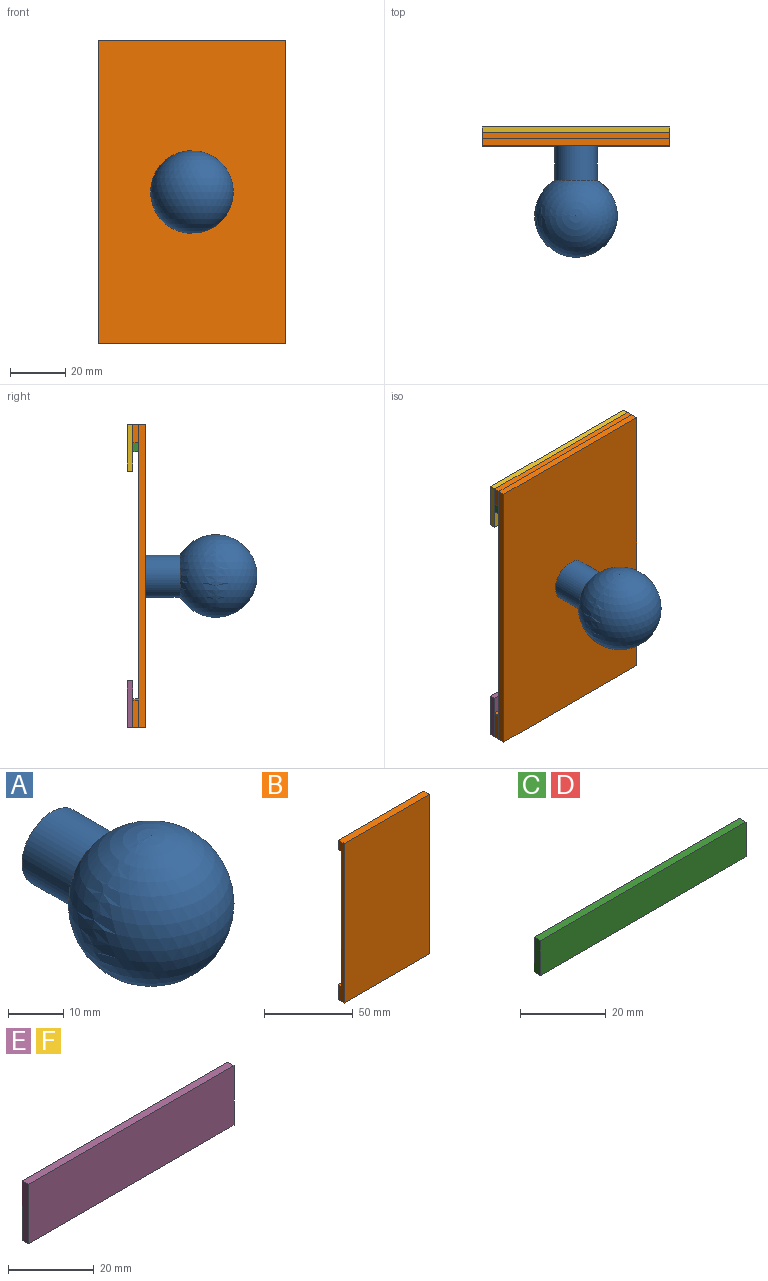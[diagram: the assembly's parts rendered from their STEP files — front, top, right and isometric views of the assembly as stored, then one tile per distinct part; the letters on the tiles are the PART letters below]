
ASSEMBLY  parts=6 mates=3
PART A: 5 faces, bbox 30x40.4x30 mm
  f0: sphere r=15mm, area 2631.4mm2, adj f1
  f1: cylinder r=7.62mm len=15.24mm, axis (0,-1,0), area 597.5mm2, adj f0,f2
  f2: plane 15.24x15.24mm, normal (0,1,0), area 182.4mm2, adj f1
  f3: sphere r=7.62mm, area 364.8mm2, adj f4
  f4: plane 15.24x15.24mm, normal (0,-1,0), area 182.4mm2, adj f3
PART B: 10 faces, bbox 68x4.6x110 mm
  f0: plane 92.79x68mm, normal (0,1,0), area 6310mm2, adj f2,f4,f6,f8
  f1: plane 68x4.64mm, normal (0,0,1), area 315.5mm2, adj f2,f4,f5,f7
  f2: plane 110x4.64mm, normal (-1,0,0), area 315.5mm2, adj f0,f1,f3,f5,f6,f7,f8,f9
  f3: plane 68x4.64mm, normal (0,0,-1), area 315.5mm2, adj f2,f4,f5,f9
  f4: plane 110x4.64mm, normal (1,0,0), area 315.5mm2, adj f0,f1,f3,f5,f6,f7,f8,f9
  f5: plane 110x68mm, normal (0,-1,0), area 7480mm2, adj f1,f2,f3,f4
  f6: plane 68x2.1mm, normal (0,0,-1), area 142.8mm2, adj f0,f2,f4,f7
  f7: plane 68x6.69mm, normal (0,1,0), area 454.8mm2, adj f1,f2,f4,f6
  f8: plane 68x2.1mm, normal (0,0,1), area 142.8mm2, adj f0,f2,f4,f9
  f9: plane 68x10.52mm, normal (0,1,0), area 715.2mm2, adj f2,f3,f4,f8
PART C: 6 faces, bbox 68x2.1x10 mm
  f0: plane 10x2.1mm, normal (-1,0,0), area 21mm2, adj f1,f3,f4,f5
  f1: plane 68x2.1mm, normal (0,0,-1), area 142.8mm2, adj f0,f2,f4,f5
  f2: plane 10x2.1mm, normal (1,0,0), area 21mm2, adj f1,f3,f4,f5
  f3: plane 68x2.1mm, normal (0,0,1), area 142.8mm2, adj f0,f2,f4,f5
  f4: plane 68x10mm, normal (0,-1,0), area 680mm2, adj f0,f1,f2,f3
  f5: plane 68x10mm, normal (0,1,0), area 680mm2, adj f0,f1,f2,f3
PART D: same geometry as C
PART E: 6 faces, bbox 68x2.1x17 mm
  f0: plane 68x2.1mm, normal (0,0,1), area 142.8mm2, adj f1,f3,f4,f5
  f1: plane 17x2.1mm, normal (-1,0,0), area 35.7mm2, adj f0,f2,f4,f5
  f2: plane 68x2.1mm, normal (0,0,-1), area 142.8mm2, adj f1,f3,f4,f5
  f3: plane 17x2.1mm, normal (1,0,0), area 35.7mm2, adj f0,f2,f4,f5
  f4: plane 68x17mm, normal (0,-1,0), area 1156mm2, adj f0,f1,f2,f3
  f5: plane 68x17mm, normal (0,1,0), area 1156mm2, adj f0,f1,f2,f3
PART F: same geometry as E
PLACE A t=(-86.53,-51.05,0.45)mm
PLACE B t=(-11.08,-23.11,11.03)mm
PLACE C t=(-11.43,-21.01,-9.27)mm
PLACE D t=(-11.43,-21.01,-109.27)mm
PLACE E t=(-100.03,-18.91,-85.83)mm
PLACE F t=(-100.03,-18.91,7.17)mm
MATE fastened A.f1 <-> B.f5  axis (0,1,0) through (-33.87,-25.65,-7.24)mm
MATE fastened F.f4 <-> C.f5  axis (0,-1,0) through (-33.87,-21.01,47.76)mm
MATE fastened E.f4 <-> D.f5  axis (0,-1,0) through (-33.87,-21.01,-62.24)mm
